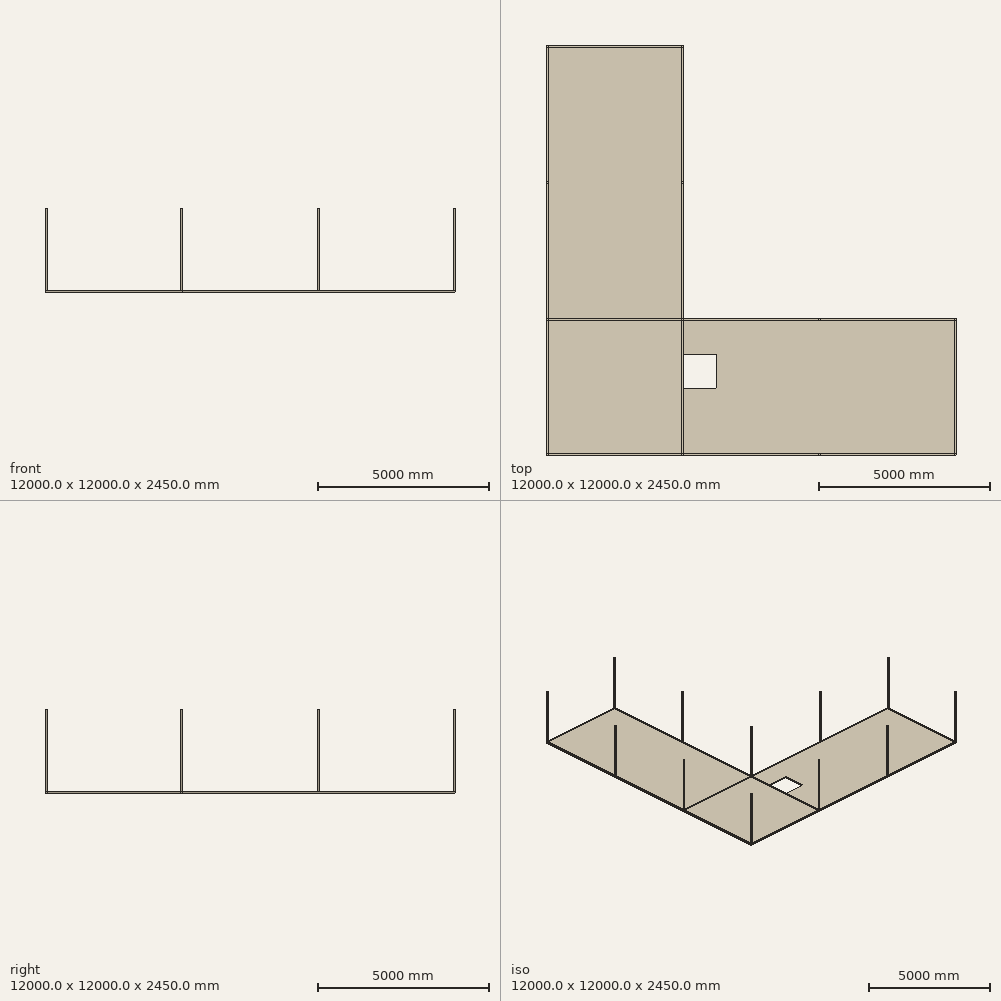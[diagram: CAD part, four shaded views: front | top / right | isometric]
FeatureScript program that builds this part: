
annotation { "Feature Type Name" : "Feature", "Feature Type Description" : "" }
export const myFeature = defineFeature(function(context is Context, id is Id, definition is map)
    precondition{}
    {
        {
            var Q0;
            Q0=qCreatedBy(makeId("Top.planeOp"),FACE);
            var sketch = newSketch(context, id + "F0", { "sketchPlane" : qUnion([Q0])});
            skLineSegment(sketch, "E0.bottom", {"start": v(0, 0) * mm, "end": v(8000, 0) * mm});
            skLineSegment(sketch, "E0.top", {"start": v(0, -50) * mm, "end": v(8000, -50) * mm});
            skLineSegment(sketch, "E0.left", {"start": v(0, 0) * mm, "end": v(0, -50) * mm});
            skLineSegment(sketch, "E0.right", {"start": v(8000, 0) * mm, "end": v(8000, -50) * mm});
            skSolve(sketch);
        }
        {
            var Q0;
            Q0=qCreatedBy(makeId("Top.planeOp"),FACE);
            var sketch = newSketch(context, id + "F1", { "sketchPlane" : qUnion([Q0])});
            skLineSegment(sketch, "E1.bottom", {"start": v(8000, -50) * mm, "end": v(7950, -50) * mm});
            skLineSegment(sketch, "E1.top", {"start": v(8000, -3950) * mm, "end": v(7950, -3950) * mm});
            skLineSegment(sketch, "E1.left", {"start": v(8000, -50) * mm, "end": v(8000, -3950) * mm});
            skLineSegment(sketch, "E1.right", {"start": v(7950, -50) * mm, "end": v(7950, -3950) * mm});
            skSolve(sketch);
        }
        {
            var Q0;
            Q0=qCreatedBy(makeId("Top.planeOp"),FACE);
            var sketch = newSketch(context, id + "F2", { "sketchPlane" : qUnion([Q0])});
            skLineSegment(sketch, "E2.bottom", {"start": v(8000, -3950) * mm, "end": v(0, -3950) * mm});
            skLineSegment(sketch, "E2.top", {"start": v(8000, -4000) * mm, "end": v(0, -4000) * mm});
            skLineSegment(sketch, "E2.left", {"start": v(8000, -3950) * mm, "end": v(8000, -4000) * mm});
            skLineSegment(sketch, "E2.right", {"start": v(0, -3950) * mm, "end": v(0, -4000) * mm});
            skSolve(sketch);
        }
        {
            var Q0;
            Q0=qCreatedBy(makeId("Top.planeOp"),FACE);
            var sketch = newSketch(context, id + "F3", { "sketchPlane" : qUnion([Q0])});
            skLineSegment(sketch, "E3.bottom", {"start": v(0, 0) * mm, "end": v(-50, 0) * mm});
            skLineSegment(sketch, "E3.top", {"start": v(0, 8000) * mm, "end": v(-50, 8000) * mm});
            skLineSegment(sketch, "E3.left", {"start": v(0, 0) * mm, "end": v(0, 8000) * mm});
            skLineSegment(sketch, "E3.right", {"start": v(-50, 0) * mm, "end": v(-50, 8000) * mm});
            skSolve(sketch);
        }
        {
            var Q0;
            Q0=qCreatedBy(makeId("Top.planeOp"),FACE);
            var sketch = newSketch(context, id + "F4", { "sketchPlane" : qUnion([Q0])});
            skLineSegment(sketch, "E4.bottom", {"start": v(-50, 8000) * mm, "end": v(-3950, 8000) * mm});
            skLineSegment(sketch, "E4.top", {"start": v(-50, 7950) * mm, "end": v(-3950, 7950) * mm});
            skLineSegment(sketch, "E4.left", {"start": v(-50, 8000) * mm, "end": v(-50, 7950) * mm});
            skLineSegment(sketch, "E4.right", {"start": v(-3950, 8000) * mm, "end": v(-3950, 7950) * mm});
            skSolve(sketch);
        }
        {
            var Q0;
            Q0=qCreatedBy(makeId("Top.planeOp"),FACE);
            var sketch = newSketch(context, id + "F5", { "sketchPlane" : qUnion([Q0])});
            skLineSegment(sketch, "E5.bottom", {"start": v(-3950, 8000) * mm, "end": v(-4000, 8000) * mm});
            skLineSegment(sketch, "E5.top", {"start": v(-3950, 0) * mm, "end": v(-4000, 0) * mm});
            skLineSegment(sketch, "E5.left", {"start": v(-3950, 8000) * mm, "end": v(-3950, 0) * mm});
            skLineSegment(sketch, "E5.right", {"start": v(-4000, 8000) * mm, "end": v(-4000, 0) * mm});
            skSolve(sketch);
        }
        {
            var Q0;
            Q0=qCreatedBy(makeId("Top.planeOp"),FACE);
            var sketch = newSketch(context, id + "F6", { "sketchPlane" : qUnion([Q0])});
            skLineSegment(sketch, "E6.bottom", {"start": v(0, -4000) * mm, "end": v(-4000, -4000) * mm});
            skLineSegment(sketch, "E6.top", {"start": v(0, -3950) * mm, "end": v(-4000, -3950) * mm});
            skLineSegment(sketch, "E6.left", {"start": v(0, -4000) * mm, "end": v(0, -3950) * mm});
            skLineSegment(sketch, "E6.right", {"start": v(-4000, -4000) * mm, "end": v(-4000, -3950) * mm});
            skSolve(sketch);
        }
        {
            var Q0;
            Q0=qCreatedBy(makeId("Top.planeOp"),FACE);
            var sketch = newSketch(context, id + "F7", { "sketchPlane" : qUnion([Q0])});
            skLineSegment(sketch, "E7.bottom", {"start": v(0, 0) * mm, "end": v(-4000, 0) * mm});
            skLineSegment(sketch, "E7.top", {"start": v(0, -50) * mm, "end": v(-4000, -50) * mm});
            skLineSegment(sketch, "E7.left", {"start": v(0, 0) * mm, "end": v(0, -50) * mm});
            skLineSegment(sketch, "E7.right", {"start": v(-4000, 0) * mm, "end": v(-4000, -50) * mm});
            skSolve(sketch);
        }
        {
            var Q0;
            Q0=qCreatedBy(makeId("Top.planeOp"),FACE);
            var sketch = newSketch(context, id + "F8", { "sketchPlane" : qUnion([Q0])});
            skLineSegment(sketch, "E8.bottom", {"start": v(-4000, -50) * mm, "end": v(-3950, -50) * mm});
            skLineSegment(sketch, "E8.top", {"start": v(-4000, -3950) * mm, "end": v(-3950, -3950) * mm});
            skLineSegment(sketch, "E8.left", {"start": v(-4000, -50) * mm, "end": v(-4000, -3950) * mm});
            skLineSegment(sketch, "E8.right", {"start": v(-3950, -50) * mm, "end": v(-3950, -3950) * mm});
            skSolve(sketch);
        }
        {
            var Q0;
            Q0=qCreatedBy(makeId("Top.planeOp"),FACE);
            var sketch = newSketch(context, id + "F9", { "sketchPlane" : qUnion([Q0])});
            skLineSegment(sketch, "E9.bottom", {"start": v(0, -50) * mm, "end": v(-50, -50) * mm});
            skLineSegment(sketch, "E9.top", {"start": v(0, -3950) * mm, "end": v(-50, -3950) * mm});
            skLineSegment(sketch, "E9.left", {"start": v(0, -50) * mm, "end": v(0, -3950) * mm});
            skLineSegment(sketch, "E9.right", {"start": v(-50, -50) * mm, "end": v(-50, -3950) * mm});
            skSolve(sketch);
        }
        {
            var Q0;
            Q0=qCreatedBy(makeId("Top.planeOp"),FACE);
            var sketch = newSketch(context, id + "F10", { "sketchPlane" : qUnion([Q0])});
            skLineSegment(sketch, "E10.bottom", {"start": v(-50, 0) * mm, "end": v(-1025, 0) * mm});
            skLineSegment(sketch, "E10.top", {"start": v(-50, 993.75) * mm, "end": v(-1025, 993.75) * mm});
            skLineSegment(sketch, "E10.left", {"start": v(-50, 0) * mm, "end": v(-50, 993.75) * mm});
            skLineSegment(sketch, "E10.right", {"start": v(-1025, 0) * mm, "end": v(-1025, 993.75) * mm});
            skLineSegment(sketch, "E11.bottom", {"start": v(-1025, 0) * mm, "end": v(-2000, 0) * mm});
            skLineSegment(sketch, "E11.top", {"start": v(-1025, 993.75) * mm, "end": v(-2000, 993.75) * mm});
            skLineSegment(sketch, "E11.right", {"start": v(-2000, 0) * mm, "end": v(-2000, 993.75) * mm});
            skLineSegment(sketch, "E12.bottom", {"start": v(-2000, 0) * mm, "end": v(-2975, 0) * mm});
            skLineSegment(sketch, "E12.top", {"start": v(-2000, 993.75) * mm, "end": v(-2975, 993.75) * mm});
            skLineSegment(sketch, "E12.right", {"start": v(-2975, 0) * mm, "end": v(-2975, 993.75) * mm});
            skLineSegment(sketch, "E13.bottom", {"start": v(-2975, 0) * mm, "end": v(-3950, 0) * mm});
            skLineSegment(sketch, "E13.top", {"start": v(-2975, 993.75) * mm, "end": v(-3950, 993.75) * mm});
            skLineSegment(sketch, "E13.right", {"start": v(-3950, 0) * mm, "end": v(-3950, 993.75) * mm});
            skLineSegment(sketch, "E14.top", {"start": v(-50, 1987.5) * mm, "end": v(-1025, 1987.5) * mm});
            skLineSegment(sketch, "E14.left", {"start": v(-50, 993.75) * mm, "end": v(-50, 1987.5) * mm});
            skLineSegment(sketch, "E14.right", {"start": v(-1025, 993.75) * mm, "end": v(-1025, 1987.5) * mm});
            skLineSegment(sketch, "E15.top", {"start": v(-1025, 1987.5) * mm, "end": v(-2000, 1987.5) * mm});
            skLineSegment(sketch, "E15.right", {"start": v(-2000, 993.75) * mm, "end": v(-2000, 1987.5) * mm});
            skLineSegment(sketch, "E16.top", {"start": v(-2000, 1987.5) * mm, "end": v(-2975, 1987.5) * mm});
            skLineSegment(sketch, "E16.right", {"start": v(-2975, 993.75) * mm, "end": v(-2975, 1987.5) * mm});
            skLineSegment(sketch, "E17.top", {"start": v(-2975, 1987.5) * mm, "end": v(-3950, 1987.5) * mm});
            skLineSegment(sketch, "E17.right", {"start": v(-3950, 993.75) * mm, "end": v(-3950, 1987.5) * mm});
            skLineSegment(sketch, "E18.top", {"start": v(-50, 2981.25) * mm, "end": v(-1025, 2981.25) * mm});
            skLineSegment(sketch, "E18.left", {"start": v(-50, 1987.5) * mm, "end": v(-50, 2981.25) * mm});
            skLineSegment(sketch, "E18.right", {"start": v(-1025, 1987.5) * mm, "end": v(-1025, 2981.25) * mm});
            skLineSegment(sketch, "E19.top", {"start": v(-1025, 2981.25) * mm, "end": v(-2000, 2981.25) * mm});
            skLineSegment(sketch, "E19.right", {"start": v(-2000, 1987.5) * mm, "end": v(-2000, 2981.25) * mm});
            skLineSegment(sketch, "E20.top", {"start": v(-2000, 2981.25) * mm, "end": v(-2975, 2981.25) * mm});
            skLineSegment(sketch, "E20.right", {"start": v(-2975, 1987.5) * mm, "end": v(-2975, 2981.25) * mm});
            skLineSegment(sketch, "E21.top", {"start": v(-2975, 2981.25) * mm, "end": v(-3950, 2981.25) * mm});
            skLineSegment(sketch, "E21.right", {"start": v(-3950, 1987.5) * mm, "end": v(-3950, 2981.25) * mm});
            skLineSegment(sketch, "E22.top", {"start": v(-50, 3975) * mm, "end": v(-1025, 3975) * mm});
            skLineSegment(sketch, "E22.left", {"start": v(-50, 2981.25) * mm, "end": v(-50, 3975) * mm});
            skLineSegment(sketch, "E22.right", {"start": v(-1025, 2981.25) * mm, "end": v(-1025, 3975) * mm});
            skLineSegment(sketch, "E23.top", {"start": v(-1025, 3975) * mm, "end": v(-2000, 3975) * mm});
            skLineSegment(sketch, "E23.right", {"start": v(-2000, 2981.25) * mm, "end": v(-2000, 3975) * mm});
            skLineSegment(sketch, "E24.top", {"start": v(-2000, 3975) * mm, "end": v(-2975, 3975) * mm});
            skLineSegment(sketch, "E24.right", {"start": v(-2975, 2981.25) * mm, "end": v(-2975, 3975) * mm});
            skLineSegment(sketch, "E25.top", {"start": v(-2975, 3975) * mm, "end": v(-3950, 3975) * mm});
            skLineSegment(sketch, "E25.right", {"start": v(-3950, 2981.25) * mm, "end": v(-3950, 3975) * mm});
            skLineSegment(sketch, "E26.top", {"start": v(-50, 4968.75) * mm, "end": v(-1025, 4968.75) * mm});
            skLineSegment(sketch, "E26.left", {"start": v(-50, 3975) * mm, "end": v(-50, 4968.75) * mm});
            skLineSegment(sketch, "E26.right", {"start": v(-1025, 3975) * mm, "end": v(-1025, 4968.75) * mm});
            skLineSegment(sketch, "E27.top", {"start": v(-1025, 4968.75) * mm, "end": v(-2000, 4968.75) * mm});
            skLineSegment(sketch, "E27.right", {"start": v(-2000, 3975) * mm, "end": v(-2000, 4968.75) * mm});
            skLineSegment(sketch, "E28.top", {"start": v(-2000, 4968.75) * mm, "end": v(-2975, 4968.75) * mm});
            skLineSegment(sketch, "E28.right", {"start": v(-2975, 3975) * mm, "end": v(-2975, 4968.75) * mm});
            skLineSegment(sketch, "E29.top", {"start": v(-2975, 4968.75) * mm, "end": v(-3950, 4968.75) * mm});
            skLineSegment(sketch, "E29.right", {"start": v(-3950, 3975) * mm, "end": v(-3950, 4968.75) * mm});
            skLineSegment(sketch, "E30.top", {"start": v(-50, 5962.5) * mm, "end": v(-1025, 5962.5) * mm});
            skLineSegment(sketch, "E30.left", {"start": v(-50, 4968.75) * mm, "end": v(-50, 5962.5) * mm});
            skLineSegment(sketch, "E30.right", {"start": v(-1025, 4968.75) * mm, "end": v(-1025, 5962.5) * mm});
            skLineSegment(sketch, "E31.top", {"start": v(-1025, 5962.5) * mm, "end": v(-2000, 5962.5) * mm});
            skLineSegment(sketch, "E31.right", {"start": v(-2000, 4968.75) * mm, "end": v(-2000, 5962.5) * mm});
            skLineSegment(sketch, "E32.top", {"start": v(-2000, 5962.5) * mm, "end": v(-2975, 5962.5) * mm});
            skLineSegment(sketch, "E32.right", {"start": v(-2975, 4968.75) * mm, "end": v(-2975, 5962.5) * mm});
            skLineSegment(sketch, "E33.top", {"start": v(-2975, 5962.5) * mm, "end": v(-3950, 5962.5) * mm});
            skLineSegment(sketch, "E33.right", {"start": v(-3950, 4968.75) * mm, "end": v(-3950, 5962.5) * mm});
            skLineSegment(sketch, "E34.top", {"start": v(-50, 6956.25) * mm, "end": v(-1025, 6956.25) * mm});
            skLineSegment(sketch, "E34.left", {"start": v(-50, 5962.5) * mm, "end": v(-50, 6956.25) * mm});
            skLineSegment(sketch, "E34.right", {"start": v(-1025, 5962.5) * mm, "end": v(-1025, 6956.25) * mm});
            skLineSegment(sketch, "E35.top", {"start": v(-1025, 6956.25) * mm, "end": v(-2000, 6956.25) * mm});
            skLineSegment(sketch, "E35.right", {"start": v(-2000, 5962.5) * mm, "end": v(-2000, 6956.25) * mm});
            skLineSegment(sketch, "E36.top", {"start": v(-2000, 6956.25) * mm, "end": v(-2975, 6956.25) * mm});
            skLineSegment(sketch, "E36.right", {"start": v(-2975, 5962.5) * mm, "end": v(-2975, 6956.25) * mm});
            skLineSegment(sketch, "E37.top", {"start": v(-2975, 6956.25) * mm, "end": v(-3950, 6956.25) * mm});
            skLineSegment(sketch, "E37.right", {"start": v(-3950, 5962.5) * mm, "end": v(-3950, 6956.25) * mm});
            skLineSegment(sketch, "E38.top", {"start": v(-50, 7950) * mm, "end": v(-1025, 7950) * mm});
            skLineSegment(sketch, "E38.left", {"start": v(-50, 6956.25) * mm, "end": v(-50, 7950) * mm});
            skLineSegment(sketch, "E38.right", {"start": v(-1025, 6956.25) * mm, "end": v(-1025, 7950) * mm});
            skPoint(sketch, "E39.oppositeSnap0", {"position": v(-537.5, 7950) * mm});
            skLineSegment(sketch, "E39.top", {"start": v(-1025, 7950) * mm, "end": v(-2000, 7950) * mm});
            skLineSegment(sketch, "E39.right", {"start": v(-2000, 6956.25) * mm, "end": v(-2000, 7950) * mm});
            skLineSegment(sketch, "E40.top", {"start": v(-2000, 7950) * mm, "end": v(-2975, 7950) * mm});
            skLineSegment(sketch, "E40.right", {"start": v(-2975, 6956.25) * mm, "end": v(-2975, 7950) * mm});
            skLineSegment(sketch, "E41.top", {"start": v(-2975, 7950) * mm, "end": v(-3950, 7950) * mm});
            skLineSegment(sketch, "E41.right", {"start": v(-3950, 6956.25) * mm, "end": v(-3950, 7950) * mm});
            skLineSegment(sketch, "E42.bottom", {"start": v(-50, -50) * mm, "end": v(-1025, -50) * mm});
            skLineSegment(sketch, "E42.top", {"start": v(-50, -1043.75) * mm, "end": v(-1025, -1043.75) * mm});
            skLineSegment(sketch, "E42.left", {"start": v(-50, -50) * mm, "end": v(-50, -1043.75) * mm});
            skLineSegment(sketch, "E42.right", {"start": v(-1025, -50) * mm, "end": v(-1025, -1043.75) * mm});
            skLineSegment(sketch, "E43.bottom", {"start": v(-1025, -50) * mm, "end": v(-2000, -50) * mm});
            skLineSegment(sketch, "E43.top", {"start": v(-1025, -1043.75) * mm, "end": v(-2000, -1043.75) * mm});
            skLineSegment(sketch, "E43.right", {"start": v(-2000, -50) * mm, "end": v(-2000, -1043.75) * mm});
            skLineSegment(sketch, "E44.bottom", {"start": v(-2000, -50) * mm, "end": v(-2975, -50) * mm});
            skLineSegment(sketch, "E44.top", {"start": v(-2000, -1043.75) * mm, "end": v(-2975, -1043.75) * mm});
            skLineSegment(sketch, "E44.right", {"start": v(-2975, -50) * mm, "end": v(-2975, -1043.75) * mm});
            skLineSegment(sketch, "E45.bottom", {"start": v(-2975, -50) * mm, "end": v(-3950, -50) * mm});
            skLineSegment(sketch, "E45.top", {"start": v(-2975, -1043.75) * mm, "end": v(-3950, -1043.75) * mm});
            skLineSegment(sketch, "E45.right", {"start": v(-3950, -50) * mm, "end": v(-3950, -1043.75) * mm});
            skLineSegment(sketch, "E46.top", {"start": v(-50, -2037.5) * mm, "end": v(-1025, -2037.5) * mm});
            skLineSegment(sketch, "E46.left", {"start": v(-50, -1043.75) * mm, "end": v(-50, -2037.5) * mm});
            skLineSegment(sketch, "E46.right", {"start": v(-1025, -1043.75) * mm, "end": v(-1025, -2037.5) * mm});
            skLineSegment(sketch, "E47.top", {"start": v(-1025, -2037.5) * mm, "end": v(-2000, -2037.5) * mm});
            skLineSegment(sketch, "E47.right", {"start": v(-2000, -1043.75) * mm, "end": v(-2000, -2037.5) * mm});
            skLineSegment(sketch, "E48.top", {"start": v(-2000, -2037.5) * mm, "end": v(-2975, -2037.5) * mm});
            skLineSegment(sketch, "E48.right", {"start": v(-2975, -1043.75) * mm, "end": v(-2975, -2037.5) * mm});
            skLineSegment(sketch, "E49.top", {"start": v(-2975, -2037.5) * mm, "end": v(-3950, -2037.5) * mm});
            skLineSegment(sketch, "E49.right", {"start": v(-3950, -1043.75) * mm, "end": v(-3950, -2037.5) * mm});
            skLineSegment(sketch, "E50.top", {"start": v(-50, -3031.25) * mm, "end": v(-1025, -3031.25) * mm});
            skLineSegment(sketch, "E50.left", {"start": v(-50, -2037.5) * mm, "end": v(-50, -3031.25) * mm});
            skLineSegment(sketch, "E50.right", {"start": v(-1025, -2037.5) * mm, "end": v(-1025, -3031.25) * mm});
            skLineSegment(sketch, "E51.top", {"start": v(-1025, -3031.25) * mm, "end": v(-2000, -3031.25) * mm});
            skLineSegment(sketch, "E51.right", {"start": v(-2000, -2037.5) * mm, "end": v(-2000, -3031.25) * mm});
            skLineSegment(sketch, "E52.top", {"start": v(-2000, -3031.25) * mm, "end": v(-2975, -3031.25) * mm});
            skLineSegment(sketch, "E52.right", {"start": v(-2975, -2037.5) * mm, "end": v(-2975, -3031.25) * mm});
            skLineSegment(sketch, "E53.top", {"start": v(-2975, -3031.25) * mm, "end": v(-3950, -3031.25) * mm});
            skLineSegment(sketch, "E53.right", {"start": v(-3950, -2037.5) * mm, "end": v(-3950, -3031.25) * mm});
            skLineSegment(sketch, "E54.top", {"start": v(-50, -3950) * mm, "end": v(-1025, -3950) * mm});
            skLineSegment(sketch, "E54.left", {"start": v(-50, -3031.25) * mm, "end": v(-50, -3950) * mm});
            skLineSegment(sketch, "E54.right", {"start": v(-1025, -3031.25) * mm, "end": v(-1025, -3950) * mm});
            skLineSegment(sketch, "E55.bottom", {"start": v(-1025, -3950) * mm, "end": v(-2000, -3950) * mm});
            skLineSegment(sketch, "E55.left", {"start": v(-1025, -3950) * mm, "end": v(-1025, -3031.25) * mm});
            skLineSegment(sketch, "E55.right", {"start": v(-2000, -3950) * mm, "end": v(-2000, -3031.25) * mm});
            skLineSegment(sketch, "E56.bottom", {"start": v(-2000, -3950) * mm, "end": v(-2975, -3950) * mm});
            skLineSegment(sketch, "E56.right", {"start": v(-2975, -3950) * mm, "end": v(-2975, -3031.25) * mm});
            skLineSegment(sketch, "E57.bottom", {"start": v(-2975, -3950) * mm, "end": v(-3950, -3950) * mm});
            skLineSegment(sketch, "E57.right", {"start": v(-3950, -3950) * mm, "end": v(-3950, -3031.25) * mm});
            skLineSegment(sketch, "E58.bottom", {"start": v(975, -1043.75) * mm, "end": v(0, -1043.75) * mm});
            skLineSegment(sketch, "E58.top", {"start": v(975, -50) * mm, "end": v(0, -50) * mm});
            skLineSegment(sketch, "E58.left", {"start": v(975, -1043.75) * mm, "end": v(975, -50) * mm});
            skLineSegment(sketch, "E58.right", {"start": v(0, -1043.75) * mm, "end": v(0, -50) * mm});
            skLineSegment(sketch, "E59.bottom", {"start": v(0, -1043.75) * mm, "end": v(975, -1043.75) * mm});
            skLineSegment(sketch, "E59.top", {"start": v(0, -2037.5) * mm, "end": v(975, -2037.5) * mm});
            skLineSegment(sketch, "E59.left", {"start": v(0, -1043.75) * mm, "end": v(0, -2037.5) * mm});
            skLineSegment(sketch, "E59.right", {"start": v(975, -1043.75) * mm, "end": v(975, -2037.5) * mm});
            skLineSegment(sketch, "E60.top", {"start": v(0, -3031.25) * mm, "end": v(975, -3031.25) * mm});
            skLineSegment(sketch, "E60.left", {"start": v(0, -2037.5) * mm, "end": v(0, -3031.25) * mm});
            skLineSegment(sketch, "E60.right", {"start": v(975, -2037.5) * mm, "end": v(975, -3031.25) * mm});
            skLineSegment(sketch, "E61.top", {"start": v(0, -3950) * mm, "end": v(975, -3950) * mm});
            skLineSegment(sketch, "E61.left", {"start": v(0, -3031.25) * mm, "end": v(0, -3950) * mm});
            skLineSegment(sketch, "E61.right", {"start": v(975, -3031.25) * mm, "end": v(975, -3950) * mm});
            skLineSegment(sketch, "E62.bottom", {"start": v(975, -50) * mm, "end": v(1950, -50) * mm});
            skLineSegment(sketch, "E62.top", {"start": v(975, -1043.75) * mm, "end": v(1950, -1043.75) * mm});
            skLineSegment(sketch, "E62.left", {"start": v(975, -50) * mm, "end": v(975, -1043.75) * mm});
            skLineSegment(sketch, "E62.right", {"start": v(1950, -50) * mm, "end": v(1950, -1043.75) * mm});
            skLineSegment(sketch, "E63.top", {"start": v(975, -2037.5) * mm, "end": v(1950, -2037.5) * mm});
            skLineSegment(sketch, "E63.right", {"start": v(1950, -1043.75) * mm, "end": v(1950, -2037.5) * mm});
            skLineSegment(sketch, "E64.top", {"start": v(975, -3031.25) * mm, "end": v(1950, -3031.25) * mm});
            skLineSegment(sketch, "E64.right", {"start": v(1950, -2037.5) * mm, "end": v(1950, -3031.25) * mm});
            skLineSegment(sketch, "E65.top", {"start": v(975, -3950) * mm, "end": v(1950, -3950) * mm});
            skLineSegment(sketch, "E65.right", {"start": v(1950, -3031.25) * mm, "end": v(1950, -3950) * mm});
            skLineSegment(sketch, "E66.bottom", {"start": v(1950, -50) * mm, "end": v(2925, -50) * mm});
            skLineSegment(sketch, "E66.top", {"start": v(1950, -1043.75) * mm, "end": v(2925, -1043.75) * mm});
            skLineSegment(sketch, "E66.right", {"start": v(2925, -50) * mm, "end": v(2925, -1043.75) * mm});
            skLineSegment(sketch, "E67.top", {"start": v(1950, -2037.5) * mm, "end": v(2925, -2037.5) * mm});
            skLineSegment(sketch, "E67.right", {"start": v(2925, -1043.75) * mm, "end": v(2925, -2037.5) * mm});
            skLineSegment(sketch, "E68.top", {"start": v(1950, -3031.25) * mm, "end": v(2925, -3031.25) * mm});
            skLineSegment(sketch, "E68.right", {"start": v(2925, -2037.5) * mm, "end": v(2925, -3031.25) * mm});
            skLineSegment(sketch, "E69.top", {"start": v(1950, -3950) * mm, "end": v(2925, -3950) * mm});
            skLineSegment(sketch, "E69.right", {"start": v(2925, -3031.25) * mm, "end": v(2925, -3950) * mm});
            skLineSegment(sketch, "E70.bottom", {"start": v(2925, -50) * mm, "end": v(3900, -50) * mm});
            skLineSegment(sketch, "E70.top", {"start": v(2925, -1043.75) * mm, "end": v(3900, -1043.75) * mm});
            skLineSegment(sketch, "E70.right", {"start": v(3900, -50) * mm, "end": v(3900, -1043.75) * mm});
            skLineSegment(sketch, "E71.top", {"start": v(2925, -2037.5) * mm, "end": v(3900, -2037.5) * mm});
            skLineSegment(sketch, "E71.right", {"start": v(3900, -1043.75) * mm, "end": v(3900, -2037.5) * mm});
            skLineSegment(sketch, "E72.top", {"start": v(2925, -3031.25) * mm, "end": v(3900, -3031.25) * mm});
            skLineSegment(sketch, "E72.right", {"start": v(3900, -2037.5) * mm, "end": v(3900, -3031.25) * mm});
            skLineSegment(sketch, "E73.top", {"start": v(2925, -3950) * mm, "end": v(3900, -3950) * mm});
            skLineSegment(sketch, "E73.right", {"start": v(3900, -3031.25) * mm, "end": v(3900, -3950) * mm});
            skLineSegment(sketch, "E74.bottom", {"start": v(3900, -50) * mm, "end": v(4875, -50) * mm});
            skLineSegment(sketch, "E74.top", {"start": v(3900, -1043.75) * mm, "end": v(4875, -1043.75) * mm});
            skLineSegment(sketch, "E74.right", {"start": v(4875, -50) * mm, "end": v(4875, -1043.75) * mm});
            skLineSegment(sketch, "E75.top", {"start": v(3900, -2037.5) * mm, "end": v(4875, -2037.5) * mm});
            skLineSegment(sketch, "E75.right", {"start": v(4875, -1043.75) * mm, "end": v(4875, -2037.5) * mm});
            skLineSegment(sketch, "E76.top", {"start": v(3900, -3031.25) * mm, "end": v(4875, -3031.25) * mm});
            skLineSegment(sketch, "E76.right", {"start": v(4875, -2037.5) * mm, "end": v(4875, -3031.25) * mm});
            skLineSegment(sketch, "E77.top", {"start": v(3900, -3950) * mm, "end": v(4875, -3950) * mm});
            skLineSegment(sketch, "E77.right", {"start": v(4875, -3031.25) * mm, "end": v(4875, -3950) * mm});
            skLineSegment(sketch, "E78.bottom", {"start": v(4875, -50) * mm, "end": v(5850, -50) * mm});
            skLineSegment(sketch, "E78.top", {"start": v(4875, -1043.75) * mm, "end": v(5850, -1043.75) * mm});
            skLineSegment(sketch, "E78.right", {"start": v(5850, -50) * mm, "end": v(5850, -1043.75) * mm});
            skLineSegment(sketch, "E79.top", {"start": v(4875, -2037.5) * mm, "end": v(5850, -2037.5) * mm});
            skLineSegment(sketch, "E79.right", {"start": v(5850, -1043.75) * mm, "end": v(5850, -2037.5) * mm});
            skLineSegment(sketch, "E80.top", {"start": v(4875, -3031.25) * mm, "end": v(5850, -3031.25) * mm});
            skLineSegment(sketch, "E80.right", {"start": v(5850, -2037.5) * mm, "end": v(5850, -3031.25) * mm});
            skLineSegment(sketch, "E81.top", {"start": v(4875, -3950) * mm, "end": v(5850, -3950) * mm});
            skLineSegment(sketch, "E81.right", {"start": v(5850, -3031.25) * mm, "end": v(5850, -3950) * mm});
            skLineSegment(sketch, "E82.bottom", {"start": v(5850, -50) * mm, "end": v(6825, -50) * mm});
            skLineSegment(sketch, "E82.top", {"start": v(5850, -1043.75) * mm, "end": v(6825, -1043.75) * mm});
            skLineSegment(sketch, "E82.right", {"start": v(6825, -50) * mm, "end": v(6825, -1043.75) * mm});
            skLineSegment(sketch, "E83.top", {"start": v(5850, -2037.5) * mm, "end": v(6825, -2037.5) * mm});
            skLineSegment(sketch, "E83.right", {"start": v(6825, -1043.75) * mm, "end": v(6825, -2037.5) * mm});
            skLineSegment(sketch, "E84.top", {"start": v(5850, -3031.25) * mm, "end": v(6825, -3031.25) * mm});
            skLineSegment(sketch, "E84.right", {"start": v(6825, -2037.5) * mm, "end": v(6825, -3031.25) * mm});
            skLineSegment(sketch, "E85.top", {"start": v(5850, -3950) * mm, "end": v(6825, -3950) * mm});
            skLineSegment(sketch, "E85.right", {"start": v(6825, -3031.25) * mm, "end": v(6825, -3950) * mm});
            skLineSegment(sketch, "E86.bottom", {"start": v(6825, -3031.25) * mm, "end": v(7950, -3031.25) * mm});
            skLineSegment(sketch, "E86.top", {"start": v(6825, -3950) * mm, "end": v(7950, -3950) * mm});
            skLineSegment(sketch, "E86.right", {"start": v(7950, -3031.25) * mm, "end": v(7950, -3950) * mm});
            skLineSegment(sketch, "E87.bottom", {"start": v(6825, -2037.5) * mm, "end": v(7950, -2037.5) * mm});
            skLineSegment(sketch, "E87.right", {"start": v(7950, -2037.5) * mm, "end": v(7950, -3031.25) * mm});
            skLineSegment(sketch, "E88.bottom", {"start": v(6825, -1043.75) * mm, "end": v(7950, -1043.75) * mm});
            skLineSegment(sketch, "E88.right", {"start": v(7950, -1043.75) * mm, "end": v(7950, -2037.5) * mm});
            skLineSegment(sketch, "E89.bottom", {"start": v(6825, -50) * mm, "end": v(7950, -50) * mm});
            skLineSegment(sketch, "E89.right", {"start": v(7950, -50) * mm, "end": v(7950, -1043.75) * mm});
            skSolve(sketch);
        }
        {
            var Q0;
            Q0=makeQuery(id+"F10.imprint","IMPRINT",FACE,{"disambiguationData":[TD([[makeQuery(id+"F10.imprint","IMPRINT",EDGE,{"derivedFrom":sQuery(id+"F10.wireOp",EDGE,"E79.top")}),-1.0]])]});
            var Q1;
            Q1=makeQuery(id+"F10.imprint","IMPRINT",FACE,{"disambiguationData":[TD([[makeQuery(id+"F10.imprint","IMPRINT",EDGE,{"derivedFrom":sQuery(id+"F10.wireOp",EDGE,"E80.top")}),-1.0]])]});
            var Q2;
            Q2=makeQuery(id+"F10.imprint","IMPRINT",FACE,{"disambiguationData":[TD([[makeQuery(id+"F10.imprint","IMPRINT",EDGE,{"derivedFrom":sQuery(id+"F10.wireOp",EDGE,"E45.bottom")}),1.0]])]});
            var Q3;
            Q3=makeQuery(id+"F10.imprint","IMPRINT",FACE,{"disambiguationData":[TD([[makeQuery(id+"F10.imprint","IMPRINT",EDGE,{"derivedFrom":sQuery(id+"F10.wireOp",EDGE,"E30.top")}),-1.0]])]});
            var Q4;
            Q4=makeQuery(id+"F10.imprint","IMPRINT",FACE,{"disambiguationData":[TD([[makeQuery(id+"F10.imprint","IMPRINT",EDGE,{"derivedFrom":sQuery(id+"F10.wireOp",EDGE,"E70.top")}),-1.0]])]});
            var Q5;
            Q5=makeQuery(id+"F10.imprint","IMPRINT",FACE,{"disambiguationData":[TD([[makeQuery(id+"F10.imprint","IMPRINT",EDGE,{"derivedFrom":sQuery(id+"F10.wireOp",EDGE,"E10.top")}),-1.0]])]});
            var Q6;
            Q6=makeQuery(id+"F10.imprint","IMPRINT",FACE,{"disambiguationData":[TD([[makeQuery(id+"F10.imprint","IMPRINT",EDGE,{"derivedFrom":sQuery(id+"F10.wireOp",EDGE,"E23.top")}),-1.0]])]});
            var Q7;
            Q7=makeQuery(id+"F10.imprint","IMPRINT",FACE,{"disambiguationData":[TD([[makeQuery(id+"F10.imprint","IMPRINT",EDGE,{"derivedFrom":sQuery(id+"F10.wireOp",EDGE,"E43.top")}),1.0]])]});
            var Q8;
            Q8=makeQuery(id+"F10.imprint","IMPRINT",FACE,{"disambiguationData":[TD([[makeQuery(id+"F10.imprint","IMPRINT",EDGE,{"derivedFrom":sQuery(id+"F10.wireOp",EDGE,"E44.top")}),1.0]])]});
            var Q9;
            Q9=makeQuery(id+"F10.imprint","IMPRINT",FACE,{"disambiguationData":[TD([[makeQuery(id+"F10.imprint","IMPRINT",EDGE,{"derivedFrom":sQuery(id+"F10.wireOp",EDGE,"E78.bottom")}),-1.0]])]});
            var Q10;
            Q10=makeQuery(id+"F10.imprint","IMPRINT",FACE,{"disambiguationData":[TD([[makeQuery(id+"F10.imprint","IMPRINT",EDGE,{"derivedFrom":sQuery(id+"F10.wireOp",EDGE,"E35.top")}),-1.0]])]});
            var Q11;
            Q11=makeQuery(id+"F10.imprint","IMPRINT",FACE,{"disambiguationData":[TD([[makeQuery(id+"F10.imprint","IMPRINT",EDGE,{"derivedFrom":sQuery(id+"F10.wireOp",EDGE,"E11.top")}),-1.0]])]});
            var Q12;
            Q12=makeQuery(id+"F10.imprint","IMPRINT",FACE,{"disambiguationData":[TD([[makeQuery(id+"F10.imprint","IMPRINT",EDGE,{"derivedFrom":sQuery(id+"F10.wireOp",EDGE,"E56.bottom")}),-1.0]])]});
            var Q13;
            Q13=makeQuery(id+"F10.imprint","IMPRINT",FACE,{"disambiguationData":[TD([[makeQuery(id+"F10.imprint","IMPRINT",EDGE,{"derivedFrom":sQuery(id+"F10.wireOp",EDGE,"E71.top")}),-1.0]])]});
            var Q14;
            Q14=makeQuery(id+"F10.imprint","IMPRINT",FACE,{"disambiguationData":[TD([[makeQuery(id+"F10.imprint","IMPRINT",EDGE,{"derivedFrom":sQuery(id+"F10.wireOp",EDGE,"E89.bottom")}),-1.0]])]});
            var Q15;
            Q15=makeQuery(id+"F10.imprint","IMPRINT",FACE,{"disambiguationData":[TD([[makeQuery(id+"F10.imprint","IMPRINT",EDGE,{"derivedFrom":sQuery(id+"F10.wireOp",EDGE,"E66.top")}),-1.0]])]});
            var Q16;
            Q16=makeQuery(id+"F10.imprint","IMPRINT",FACE,{"disambiguationData":[TD([[makeQuery(id+"F10.imprint","IMPRINT",EDGE,{"derivedFrom":sQuery(id+"F10.wireOp",EDGE,"E68.top")}),-1.0]])]});
            var Q17;
            Q17=makeQuery(id+"F10.imprint","IMPRINT",FACE,{"disambiguationData":[TD([[makeQuery(id+"F10.imprint","IMPRINT",EDGE,{"derivedFrom":sQuery(id+"F10.wireOp",EDGE,"E26.top")}),-1.0]])]});
            var Q18;
            Q18=makeQuery(id+"F10.imprint","IMPRINT",FACE,{"disambiguationData":[TD([[makeQuery(id+"F10.imprint","IMPRINT",EDGE,{"derivedFrom":sQuery(id+"F10.wireOp",EDGE,"E21.top")}),-1.0]])]});
            var Q19;
            Q19=makeQuery(id+"F10.imprint","IMPRINT",FACE,{"disambiguationData":[TD([[makeQuery(id+"F10.imprint","IMPRINT",EDGE,{"derivedFrom":sQuery(id+"F10.wireOp",EDGE,"E63.top")}),-1.0]])]});
            var Q20;
            Q20=makeQuery(id+"F10.imprint","IMPRINT",FACE,{"disambiguationData":[TD([[makeQuery(id+"F10.imprint","IMPRINT",EDGE,{"derivedFrom":sQuery(id+"F10.wireOp",EDGE,"E42.bottom")}),1.0]])]});
            var Q21;
            Q21=makeQuery(id+"F10.imprint","IMPRINT",FACE,{"disambiguationData":[TD([[makeQuery(id+"F10.imprint","IMPRINT",EDGE,{"derivedFrom":sQuery(id+"F10.wireOp",EDGE,"E67.top")}),-1.0]])]});
            var Q22;
            Q22=makeQuery(id+"F10.imprint","IMPRINT",FACE,{"disambiguationData":[TD([[makeQuery(id+"F10.imprint","IMPRINT",EDGE,{"derivedFrom":sQuery(id+"F10.wireOp",EDGE,"E60.top")}),-1.0]])]});
            var Q23;
            Q23=makeQuery(id+"F10.imprint","IMPRINT",FACE,{"disambiguationData":[TD([[makeQuery(id+"F10.imprint","IMPRINT",EDGE,{"derivedFrom":sQuery(id+"F10.wireOp",EDGE,"E62.bottom")}),-1.0]])]});
            var Q24;
            Q24=makeQuery(id+"F10.imprint","IMPRINT",FACE,{"disambiguationData":[TD([[makeQuery(id+"F10.imprint","IMPRINT",EDGE,{"derivedFrom":sQuery(id+"F10.wireOp",EDGE,"E45.top")}),1.0]])]});
            var Q25;
            Q25=makeQuery(id+"F10.imprint","IMPRINT",FACE,{"disambiguationData":[TD([[makeQuery(id+"F10.imprint","IMPRINT",EDGE,{"derivedFrom":sQuery(id+"F10.wireOp",EDGE,"E82.bottom")}),-1.0]])]});
            var Q26;
            Q26=makeQuery(id+"F10.imprint","IMPRINT",FACE,{"disambiguationData":[TD([[makeQuery(id+"F10.imprint","IMPRINT",EDGE,{"derivedFrom":sQuery(id+"F10.wireOp",EDGE,"E14.top")}),-1.0]])]});
            var Q27;
            Q27=makeQuery(id+"F10.imprint","IMPRINT",FACE,{"disambiguationData":[TD([[makeQuery(id+"F10.imprint","IMPRINT",EDGE,{"derivedFrom":sQuery(id+"F10.wireOp",EDGE,"E33.top")}),-1.0]])]});
            var Q28;
            Q28=makeQuery(id+"F10.imprint","IMPRINT",FACE,{"disambiguationData":[TD([[makeQuery(id+"F10.imprint","IMPRINT",EDGE,{"derivedFrom":sQuery(id+"F10.wireOp",EDGE,"E58.top")}),1.0]])]});
            var Q29;
            Q29=makeQuery(id+"F10.imprint","IMPRINT",FACE,{"disambiguationData":[TD([[makeQuery(id+"F10.imprint","IMPRINT",EDGE,{"derivedFrom":sQuery(id+"F10.wireOp",EDGE,"E49.top")}),1.0]])]});
            var Q30;
            Q30=makeQuery(id+"F10.imprint","IMPRINT",FACE,{"disambiguationData":[TD([[makeQuery(id+"F10.imprint","IMPRINT",EDGE,{"derivedFrom":sQuery(id+"F10.wireOp",EDGE,"E19.top")}),-1.0]])]});
            var Q31;
            Q31=makeQuery(id+"F10.imprint","IMPRINT",FACE,{"disambiguationData":[TD([[makeQuery(id+"F10.imprint","IMPRINT",EDGE,{"derivedFrom":sQuery(id+"F10.wireOp",EDGE,"E15.top")}),-1.0]])]});
            var Q32;
            Q32=makeQuery(id+"F10.imprint","IMPRINT",FACE,{"disambiguationData":[TD([[makeQuery(id+"F10.imprint","IMPRINT",EDGE,{"derivedFrom":sQuery(id+"F10.wireOp",EDGE,"E13.bottom")}),-1.0]])]});
            var Q33;
            Q33=makeQuery(id+"F10.imprint","IMPRINT",FACE,{"disambiguationData":[TD([[makeQuery(id+"F10.imprint","IMPRINT",EDGE,{"derivedFrom":sQuery(id+"F10.wireOp",EDGE,"E43.bottom")}),1.0]])]});
            var Q34;
            Q34=makeQuery(id+"F10.imprint","IMPRINT",FACE,{"disambiguationData":[TD([[makeQuery(id+"F10.imprint","IMPRINT",EDGE,{"derivedFrom":sQuery(id+"F10.wireOp",EDGE,"E87.bottom")}),1.0]])]});
            var Q35;
            Q35=makeQuery(id+"F10.imprint","IMPRINT",FACE,{"disambiguationData":[TD([[makeQuery(id+"F10.imprint","IMPRINT",EDGE,{"derivedFrom":sQuery(id+"F10.wireOp",EDGE,"E62.top")}),-1.0]])]});
            var Q36;
            Q36=makeQuery(id+"F10.imprint","IMPRINT",FACE,{"disambiguationData":[TD([[makeQuery(id+"F10.imprint","IMPRINT",EDGE,{"derivedFrom":sQuery(id+"F10.wireOp",EDGE,"E59.top")}),-1.0]])]});
            var Q37;
            Q37=makeQuery(id+"F10.imprint","IMPRINT",FACE,{"disambiguationData":[TD([[makeQuery(id+"F10.imprint","IMPRINT",EDGE,{"derivedFrom":sQuery(id+"F10.wireOp",EDGE,"E74.top")}),-1.0]])]});
            var Q38;
            Q38=makeQuery(id+"F10.imprint","IMPRINT",FACE,{"disambiguationData":[TD([[makeQuery(id+"F10.imprint","IMPRINT",EDGE,{"derivedFrom":sQuery(id+"F10.wireOp",EDGE,"E27.top")}),-1.0]])]});
            var Q39;
            Q39=makeQuery(id+"F10.imprint","IMPRINT",FACE,{"disambiguationData":[TD([[makeQuery(id+"F10.imprint","IMPRINT",EDGE,{"derivedFrom":sQuery(id+"F10.wireOp",EDGE,"E47.top")}),1.0]])]});
            var Q40;
            Q40=makeQuery(id+"F10.imprint","IMPRINT",FACE,{"disambiguationData":[TD([[makeQuery(id+"F10.imprint","IMPRINT",EDGE,{"derivedFrom":sQuery(id+"F10.wireOp",EDGE,"E86.bottom")}),1.0]])]});
            var Q41;
            Q41=makeQuery(id+"F10.imprint","IMPRINT",FACE,{"disambiguationData":[TD([[makeQuery(id+"F10.imprint","IMPRINT",EDGE,{"derivedFrom":sQuery(id+"F10.wireOp",EDGE,"E12.bottom")}),-1.0]])]});
            var Q42;
            Q42=makeQuery(id+"F10.imprint","IMPRINT",FACE,{"disambiguationData":[TD([[makeQuery(id+"F10.imprint","IMPRINT",EDGE,{"derivedFrom":sQuery(id+"F10.wireOp",EDGE,"E37.top")}),-1.0]])]});
            var Q43;
            Q43=makeQuery(id+"F10.imprint","IMPRINT",FACE,{"disambiguationData":[TD([[makeQuery(id+"F10.imprint","IMPRINT",EDGE,{"derivedFrom":sQuery(id+"F10.wireOp",EDGE,"E34.top")}),-1.0]])]});
            var Q44;
            Q44=makeQuery(id+"F10.imprint","IMPRINT",FACE,{"disambiguationData":[TD([[makeQuery(id+"F10.imprint","IMPRINT",EDGE,{"derivedFrom":sQuery(id+"F10.wireOp",EDGE,"E74.bottom")}),-1.0]])]});
            var Q45;
            Q45=makeQuery(id+"F10.imprint","IMPRINT",FACE,{"disambiguationData":[TD([[makeQuery(id+"F10.imprint","IMPRINT",EDGE,{"derivedFrom":sQuery(id+"F10.wireOp",EDGE,"E16.top")}),-1.0]])]});
            var Q46;
            Q46=makeQuery(id+"F10.imprint","IMPRINT",FACE,{"disambiguationData":[TD([[makeQuery(id+"F10.imprint","IMPRINT",EDGE,{"derivedFrom":sQuery(id+"F10.wireOp",EDGE,"E12.top")}),-1.0]])]});
            var Q47;
            Q47=makeQuery(id+"F10.imprint","IMPRINT",FACE,{"disambiguationData":[TD([[makeQuery(id+"F10.imprint","IMPRINT",EDGE,{"derivedFrom":sQuery(id+"F10.wireOp",EDGE,"E82.top")}),-1.0]])]});
            var Q48;
            Q48=makeQuery(id+"F10.imprint","IMPRINT",FACE,{"disambiguationData":[TD([[makeQuery(id+"F10.imprint","IMPRINT",EDGE,{"derivedFrom":sQuery(id+"F10.wireOp",EDGE,"E10.bottom")}),-1.0]])]});
            var Q49;
            Q49=makeQuery(id+"F10.imprint","IMPRINT",FACE,{"disambiguationData":[TD([[makeQuery(id+"F10.imprint","IMPRINT",EDGE,{"derivedFrom":sQuery(id+"F10.wireOp",EDGE,"E44.bottom")}),1.0]])]});
            var Q50;
            Q50=makeQuery(id+"F10.imprint","IMPRINT",FACE,{"disambiguationData":[TD([[makeQuery(id+"F10.imprint","IMPRINT",EDGE,{"derivedFrom":sQuery(id+"F10.wireOp",EDGE,"E13.top")}),-1.0]])]});
            var Q51;
            Q51=makeQuery(id+"F10.imprint","IMPRINT",FACE,{"disambiguationData":[TD([[makeQuery(id+"F10.imprint","IMPRINT",EDGE,{"derivedFrom":sQuery(id+"F10.wireOp",EDGE,"E72.top")}),-1.0]])]});
            var Q52;
            Q52=makeQuery(id+"F10.imprint","IMPRINT",FACE,{"disambiguationData":[TD([[makeQuery(id+"F10.imprint","IMPRINT",EDGE,{"derivedFrom":sQuery(id+"F10.wireOp",EDGE,"E17.top")}),-1.0]])]});
            var Q53;
            Q53=makeQuery(id+"F10.imprint","IMPRINT",FACE,{"disambiguationData":[TD([[makeQuery(id+"F10.imprint","IMPRINT",EDGE,{"derivedFrom":sQuery(id+"F10.wireOp",EDGE,"E66.bottom")}),-1.0]])]});
            var Q54;
            Q54=makeQuery(id+"F10.imprint","IMPRINT",FACE,{"disambiguationData":[TD([[makeQuery(id+"F10.imprint","IMPRINT",EDGE,{"derivedFrom":sQuery(id+"F10.wireOp",EDGE,"E11.bottom")}),-1.0]])]});
            var Q55;
            Q55=makeQuery(id+"F10.imprint","IMPRINT",FACE,{"disambiguationData":[TD([[makeQuery(id+"F10.imprint","IMPRINT",EDGE,{"derivedFrom":sQuery(id+"F10.wireOp",EDGE,"E76.top")}),-1.0]])]});
            var Q56;
            Q56=makeQuery(id+"F10.imprint","IMPRINT",FACE,{"disambiguationData":[TD([[makeQuery(id+"F10.imprint","IMPRINT",EDGE,{"derivedFrom":sQuery(id+"F10.wireOp",EDGE,"E75.top")}),-1.0]])]});
            var Q57;
            Q57=makeQuery(id+"F10.imprint","IMPRINT",FACE,{"disambiguationData":[TD([[makeQuery(id+"F10.imprint","IMPRINT",EDGE,{"derivedFrom":sQuery(id+"F10.wireOp",EDGE,"E28.top")}),-1.0]])]});
            var Q58;
            Q58=makeQuery(id+"F10.imprint","IMPRINT",FACE,{"disambiguationData":[TD([[makeQuery(id+"F10.imprint","IMPRINT",EDGE,{"derivedFrom":sQuery(id+"F10.wireOp",EDGE,"E22.top")}),-1.0]])]});
            var Q59;
            Q59=makeQuery(id+"F10.imprint","IMPRINT",FACE,{"disambiguationData":[TD([[makeQuery(id+"F10.imprint","IMPRINT",EDGE,{"derivedFrom":sQuery(id+"F10.wireOp",EDGE,"E24.top")}),-1.0]])]});
            var Q60;
            Q60=makeQuery(id+"F10.imprint","IMPRINT",FACE,{"disambiguationData":[TD([[makeQuery(id+"F10.imprint","IMPRINT",EDGE,{"derivedFrom":sQuery(id+"F10.wireOp",EDGE,"E64.top")}),-1.0]])]});
            var Q61;
            Q61=makeQuery(id+"F10.imprint","IMPRINT",FACE,{"disambiguationData":[TD([[makeQuery(id+"F10.imprint","IMPRINT",EDGE,{"derivedFrom":sQuery(id+"F10.wireOp",EDGE,"E86.top")}),1.0]])]});
            var Q62;
            Q62=makeQuery(id+"F10.imprint","IMPRINT",FACE,{"disambiguationData":[TD([[makeQuery(id+"F10.imprint","IMPRINT",EDGE,{"derivedFrom":sQuery(id+"F10.wireOp",EDGE,"E55.bottom")}),-1.0]])]});
            var Q63;
            Q63=makeQuery(id+"F10.imprint","IMPRINT",FACE,{"disambiguationData":[TD([[makeQuery(id+"F10.imprint","IMPRINT",EDGE,{"derivedFrom":sQuery(id+"F10.wireOp",EDGE,"E57.bottom")}),-1.0]])]});
            var Q64;
            Q64=makeQuery(id+"F10.imprint","IMPRINT",FACE,{"disambiguationData":[TD([[makeQuery(id+"F10.imprint","IMPRINT",EDGE,{"derivedFrom":sQuery(id+"F10.wireOp",EDGE,"E36.top")}),-1.0]])]});
            var Q65;
            Q65=makeQuery(id+"F10.imprint","IMPRINT",FACE,{"disambiguationData":[TD([[makeQuery(id+"F10.imprint","IMPRINT",EDGE,{"derivedFrom":sQuery(id+"F10.wireOp",EDGE,"E18.top")}),-1.0]])]});
            var Q66;
            Q66=makeQuery(id+"F10.imprint","IMPRINT",FACE,{"disambiguationData":[TD([[makeQuery(id+"F10.imprint","IMPRINT",EDGE,{"derivedFrom":sQuery(id+"F10.wireOp",EDGE,"E20.top")}),-1.0]])]});
            var Q67;
            Q67=makeQuery(id+"F10.imprint","IMPRINT",FACE,{"disambiguationData":[TD([[makeQuery(id+"F10.imprint","IMPRINT",EDGE,{"derivedFrom":sQuery(id+"F10.wireOp",EDGE,"E31.top")}),-1.0]])]});
            var Q68;
            Q68=makeQuery(id+"F10.imprint","IMPRINT",FACE,{"disambiguationData":[TD([[makeQuery(id+"F10.imprint","IMPRINT",EDGE,{"derivedFrom":sQuery(id+"F10.wireOp",EDGE,"E29.top")}),-1.0]])]});
            var Q69;
            Q69=makeQuery(id+"F10.imprint","IMPRINT",FACE,{"disambiguationData":[TD([[makeQuery(id+"F10.imprint","IMPRINT",EDGE,{"derivedFrom":sQuery(id+"F10.wireOp",EDGE,"E46.top")}),1.0]])]});
            var Q70;
            Q70=makeQuery(id+"F10.imprint","IMPRINT",FACE,{"disambiguationData":[TD([[makeQuery(id+"F10.imprint","IMPRINT",EDGE,{"derivedFrom":sQuery(id+"F10.wireOp",EDGE,"E32.top")}),-1.0]])]});
            var Q71;
            Q71=makeQuery(id+"F10.imprint","IMPRINT",FACE,{"disambiguationData":[TD([[makeQuery(id+"F10.imprint","IMPRINT",EDGE,{"derivedFrom":sQuery(id+"F10.wireOp",EDGE,"E59.bottom")}),-1.0]])]});
            var Q72;
            Q72=makeQuery(id+"F10.imprint","IMPRINT",FACE,{"disambiguationData":[TD([[makeQuery(id+"F10.imprint","IMPRINT",EDGE,{"derivedFrom":sQuery(id+"F10.wireOp",EDGE,"E84.top")}),-1.0]])]});
            var Q73;
            Q73=makeQuery(id+"F10.imprint","IMPRINT",FACE,{"disambiguationData":[TD([[makeQuery(id+"F10.imprint","IMPRINT",EDGE,{"derivedFrom":sQuery(id+"F10.wireOp",EDGE,"E83.top")}),-1.0]])]});
            var Q74;
            Q74=makeQuery(id+"F10.imprint","IMPRINT",FACE,{"disambiguationData":[TD([[makeQuery(id+"F10.imprint","IMPRINT",EDGE,{"derivedFrom":sQuery(id+"F10.wireOp",EDGE,"E25.top")}),-1.0]])]});
            var Q75;
            Q75=makeQuery(id+"F10.imprint","IMPRINT",FACE,{"disambiguationData":[TD([[makeQuery(id+"F10.imprint","IMPRINT",EDGE,{"derivedFrom":sQuery(id+"F10.wireOp",EDGE,"E42.top")}),1.0]])]});
            var Q76;
            Q76=makeQuery(id+"F10.imprint","IMPRINT",FACE,{"disambiguationData":[TD([[makeQuery(id+"F10.imprint","IMPRINT",EDGE,{"derivedFrom":sQuery(id+"F10.wireOp",EDGE,"E50.top")}),1.0]])]});
            var Q77;
            Q77=makeQuery(id+"F10.imprint","IMPRINT",FACE,{"disambiguationData":[TD([[makeQuery(id+"F10.imprint","IMPRINT",EDGE,{"derivedFrom":sQuery(id+"F10.wireOp",EDGE,"E78.top")}),-1.0]])]});
            var Q78;
            Q78=makeQuery(id+"F10.imprint","IMPRINT",FACE,{"disambiguationData":[TD([[makeQuery(id+"F10.imprint","IMPRINT",EDGE,{"derivedFrom":sQuery(id+"F10.wireOp",EDGE,"E70.bottom")}),-1.0]])]});
            var Q79;
            Q79=makeQuery(id+"F10.imprint","IMPRINT",FACE,{"disambiguationData":[TD([[makeQuery(id+"F10.imprint","IMPRINT",EDGE,{"derivedFrom":sQuery(id+"F10.wireOp",EDGE,"E48.top")}),1.0]])]});
            var Q80;
            Q80=makeQuery(id+"F6.imprint","IMPRINT",FACE,{"disambiguationData":[TD([[makeQuery(id+"F6.imprint","IMPRINT",EDGE,{"derivedFrom":sQuery(id+"F6.wireOp",EDGE,"E6.bottom")}),-1.0]])]});
            var Q81;
            Q81=makeQuery(id+"F8.imprint","IMPRINT",FACE,{"disambiguationData":[TD([[makeQuery(id+"F8.imprint","IMPRINT",EDGE,{"derivedFrom":sQuery(id+"F8.wireOp",EDGE,"E8.bottom")}),-1.0]])]});
            var Q82;
            Q82=makeQuery(id+"F1.imprint","IMPRINT",FACE,{"disambiguationData":[TD([[makeQuery(id+"F1.imprint","IMPRINT",EDGE,{"derivedFrom":sQuery(id+"F1.wireOp",EDGE,"E1.bottom")}),1.0]])]});
            var Q83;
            Q83=makeQuery(id+"F2.imprint","IMPRINT",FACE,{"disambiguationData":[TD([[makeQuery(id+"F2.imprint","IMPRINT",EDGE,{"derivedFrom":sQuery(id+"F2.wireOp",EDGE,"E2.bottom")}),1.0]])]});
            var Q84;
            Q84=makeQuery(id+"F5.imprint","IMPRINT",FACE,{"disambiguationData":[TD([[makeQuery(id+"F5.imprint","IMPRINT",EDGE,{"derivedFrom":sQuery(id+"F5.wireOp",EDGE,"E5.bottom")}),1.0]])]});
            var Q85;
            Q85=makeQuery(id+"F0.imprint","IMPRINT",FACE,{"disambiguationData":[TD([[makeQuery(id+"F0.imprint","IMPRINT",EDGE,{"derivedFrom":sQuery(id+"F0.wireOp",EDGE,"E0.bottom")}),-1.0]])]});
            var Q86;
            Q86=makeQuery(id+"F4.imprint","IMPRINT",FACE,{"disambiguationData":[TD([[makeQuery(id+"F4.imprint","IMPRINT",EDGE,{"derivedFrom":sQuery(id+"F4.wireOp",EDGE,"E4.bottom")}),1.0]])]});
            var Q87;
            Q87=makeQuery(id+"F7.imprint","IMPRINT",FACE,{"disambiguationData":[TD([[makeQuery(id+"F7.imprint","IMPRINT",EDGE,{"derivedFrom":sQuery(id+"F7.wireOp",EDGE,"E7.bottom")}),1.0]])]});
            var Q88;
            Q88=makeQuery(id+"F3.imprint","IMPRINT",FACE,{"disambiguationData":[TD([[makeQuery(id+"F3.imprint","IMPRINT",EDGE,{"derivedFrom":sQuery(id+"F3.wireOp",EDGE,"E3.bottom")}),-1.0]])]});
            var Q89;
            Q89=makeQuery(id+"F9.imprint","IMPRINT",FACE,{"disambiguationData":[TD([[makeQuery(id+"F9.imprint","IMPRINT",EDGE,{"derivedFrom":sQuery(id+"F9.wireOp",EDGE,"E9.bottom")}),1.0]])]});
            extrude(context, id + "F11", {"entities" : qUnion([Q0, Q1, Q2, Q3, Q4, Q5, Q6, Q7, Q8, Q9, Q10, Q11, Q12, Q13, Q14, Q15, Q16, Q17, Q18, Q19, Q20, Q21, Q22, Q23, Q24, Q25, Q26, Q27, Q28, Q29, Q30, Q31, Q32, Q33, Q34, Q35, Q36, Q37, Q38, Q39, Q40, Q41, Q42, Q43, Q44, Q45, Q46, Q47, Q48, Q49, Q50, Q51, Q52, Q53, Q54, Q55, Q56, Q57, Q58, Q59, Q60, Q61, Q62, Q63, Q64, Q65, Q66, Q67, Q68, Q69, Q70, Q71, Q72, Q73, Q74, Q75, Q76, Q77, Q78, Q79, Q80, Q81, Q82, Q83, Q84, Q85, Q86, Q87, Q88, Q89]), "depth" : 50 * mm, "offsetDistance" : 25 * mm});
        }
        {
            var Q0;
            Q0=makeQuery(id+"F11.opExtrude","CAP_FACE",FACE,{"disambiguationData":[OSD([sQuery(id+"F0.wireOp",EDGE,"E0.bottom"),sQuery(id+"F0.wireOp",EDGE,"E0.top"),sQuery(id+"F0.wireOp",EDGE,"E0.left"),sQuery(id+"F0.wireOp",EDGE,"E0.right")])],"isStart":false});
            var sketch = newSketch(context, id + "F12", { "sketchPlane" : qUnion([Q0])});
            skLineSegment(sketch, "E90.bottom", {"start": v(8000, 0) * mm, "end": v(7950, 0) * mm});
            skLineSegment(sketch, "E90.top", {"start": v(8000, -50) * mm, "end": v(7950, -50) * mm});
            skLineSegment(sketch, "E90.left", {"start": v(8000, 0) * mm, "end": v(8000, -50) * mm});
            skLineSegment(sketch, "E90.right", {"start": v(7950, 0) * mm, "end": v(7950, -50) * mm});
            skLineSegment(sketch, "E91.bottom", {"start": v(8000, -4000) * mm, "end": v(7950, -4000) * mm});
            skLineSegment(sketch, "E91.top", {"start": v(8000, -3950) * mm, "end": v(7950, -3950) * mm});
            skLineSegment(sketch, "E91.left", {"start": v(8000, -4000) * mm, "end": v(8000, -3950) * mm});
            skLineSegment(sketch, "E91.right", {"start": v(7950, -4000) * mm, "end": v(7950, -3950) * mm});
            skLineSegment(sketch, "E92.bottom", {"start": v(-3950, -3950) * mm, "end": v(-4000, -3950) * mm});
            skLineSegment(sketch, "E92.top", {"start": v(-3950, -4000) * mm, "end": v(-4000, -4000) * mm});
            skLineSegment(sketch, "E92.left", {"start": v(-3950, -3950) * mm, "end": v(-3950, -4000) * mm});
            skLineSegment(sketch, "E92.right", {"start": v(-4000, -3950) * mm, "end": v(-4000, -4000) * mm});
            skLineSegment(sketch, "E93.bottom", {"start": v(0, 8000) * mm, "end": v(-50, 8000) * mm});
            skLineSegment(sketch, "E93.top", {"start": v(0, 7950) * mm, "end": v(-50, 7950) * mm});
            skLineSegment(sketch, "E93.left", {"start": v(0, 8000) * mm, "end": v(0, 7950) * mm});
            skLineSegment(sketch, "E93.right", {"start": v(-50, 8000) * mm, "end": v(-50, 7950) * mm});
            skLineSegment(sketch, "E94.bottom", {"start": v(-4000, 8000) * mm, "end": v(-3950, 8000) * mm});
            skLineSegment(sketch, "E94.top", {"start": v(-4000, 7950) * mm, "end": v(-3950, 7950) * mm});
            skLineSegment(sketch, "E94.left", {"start": v(-4000, 8000) * mm, "end": v(-4000, 7950) * mm});
            skLineSegment(sketch, "E94.right", {"start": v(-3950, 8000) * mm, "end": v(-3950, 7950) * mm});
            skLineSegment(sketch, "E95.bottom", {"start": v(0, -4000) * mm, "end": v(-50, -4000) * mm});
            skLineSegment(sketch, "E95.top", {"start": v(0, -3950) * mm, "end": v(-50, -3950) * mm});
            skLineSegment(sketch, "E95.left", {"start": v(0, -4000) * mm, "end": v(0, -3950) * mm});
            skLineSegment(sketch, "E95.right", {"start": v(-50, -4000) * mm, "end": v(-50, -3950) * mm});
            skLineSegment(sketch, "E96.bottom", {"start": v(-4000, 0) * mm, "end": v(-3950, 0) * mm});
            skLineSegment(sketch, "E96.top", {"start": v(-4000, -50) * mm, "end": v(-3950, -50) * mm});
            skLineSegment(sketch, "E96.left", {"start": v(-4000, 0) * mm, "end": v(-4000, -50) * mm});
            skLineSegment(sketch, "E96.right", {"start": v(-3950, 0) * mm, "end": v(-3950, -50) * mm});
            skLineSegment(sketch, "E97.bottom", {"start": v(0, 0) * mm, "end": v(-50, 0) * mm});
            skLineSegment(sketch, "E97.top", {"start": v(0, -50) * mm, "end": v(-50, -50) * mm});
            skLineSegment(sketch, "E97.left", {"start": v(0, 0) * mm, "end": v(0, -50) * mm});
            skLineSegment(sketch, "E97.right", {"start": v(-50, 0) * mm, "end": v(-50, -50) * mm});
            skLineSegment(sketch, "E98.bottom", {"start": v(4025, -50) * mm, "end": v(3975, -50) * mm});
            skLineSegment(sketch, "E98.top", {"start": v(4025, 0) * mm, "end": v(3975, 0) * mm});
            skLineSegment(sketch, "E98.left", {"start": v(4025, -50) * mm, "end": v(4025, 0) * mm});
            skLineSegment(sketch, "E98.right", {"start": v(3975, -50) * mm, "end": v(3975, 0) * mm});
            skLineSegment(sketch, "E99.bottom", {"start": v(4025, -3950) * mm, "end": v(3975, -3950) * mm});
            skLineSegment(sketch, "E99.top", {"start": v(4025, -4000) * mm, "end": v(3975, -4000) * mm});
            skLineSegment(sketch, "E99.left", {"start": v(4025, -3950) * mm, "end": v(4025, -4000) * mm});
            skLineSegment(sketch, "E99.right", {"start": v(3975, -3950) * mm, "end": v(3975, -4000) * mm});
            skLineSegment(sketch, "E100.bottom", {"start": v(0, 3975) * mm, "end": v(-50, 3975) * mm});
            skLineSegment(sketch, "E100.top", {"start": v(0, 4025) * mm, "end": v(-50, 4025) * mm});
            skLineSegment(sketch, "E100.left", {"start": v(0, 3975) * mm, "end": v(0, 4025) * mm});
            skLineSegment(sketch, "E100.right", {"start": v(-50, 3975) * mm, "end": v(-50, 4025) * mm});
            skPoint(sketch, "E100.middle", {"position": v(-25, 4000) * mm});
            skLineSegment(sketch, "E101.bottom", {"start": v(-3950, 4025) * mm, "end": v(-4000, 4025) * mm});
            skLineSegment(sketch, "E101.top", {"start": v(-3950, 3975) * mm, "end": v(-4000, 3975) * mm});
            skLineSegment(sketch, "E101.left", {"start": v(-3950, 4025) * mm, "end": v(-3950, 3975) * mm});
            skLineSegment(sketch, "E101.right", {"start": v(-4000, 4025) * mm, "end": v(-4000, 3975) * mm});
            skSolve(sketch);
        }
        {
            var Q0;
            Q0 = qSketchRegion(id + "F12", true);
            extrude(context, id + "F13", {"entities" : qUnion([Q0]), "depth" : 2400 * mm, "offsetDistance" : 25 * mm});
        }
    });
